# Revit family: ENCBMTYP001
name_source: partatom
category: Furniture
units: mm (PartAtom-declared; Revit-internal decimal feet)

## family parameters
Always vertical = Yes
Cut with Voids When Loaded = No
OmniClass Number = 23.40.20.00
OmniClass Title = General Furniture and Specialties
Render Appearance Source = Family Geometry
Room Calculation Point = No
Shared = No
Work Plane-Based = No

## types (1)
- ENCBMTYP001
    Default Elevation = 0 mm  [stored 0 ft]
    Description = 2 x PASS THROUGH JUMPER - AO2 8W4C - 39"(PASS THRU 30"PANEL, 6 x Black DUPLEX OUTLET LINE 1 - 8W 4C - W/SCREW, 6 x Black DUPLEX OUTLET LINE 2 - 8W 4C - W/SCREW, 1 x BASE INFEED - AO2/MWALL - 8 WIRE 4 CIRCUIT - SIDE MOUNTED, 3 x SPINE SCREEN  50H HORIZON 20H 60W, 6 x Mobile Pedestal - B/F - 24D, 3 x Encounter PwrBeam Double Sided Powered Spine Kit 60, 6 x Encounter PwrBeam Power Cord Tray 60w, 2 x Encounter PwrBeam Raceway Endcap Painted, 4 x Encounter PwrBeam 18 inch T-Leg for 21h, 1 x Encounter PwrBeam UnderMnt pole for 21h, 6 x TBL, REC, 2mm, 30Dx60Wx29H, HAL, E SERIES GLD 2 STAGE
    Exported From CET Designer = Yes
    Manufacturer = AIS
    Model = E-HM8W4PJ30
    Show ENCBMTYP001 = Yes
    VisibilityIndex = 0

note: [stored X ft] marks values corroborated as IEEE doubles in the binary element streams (Revit-internal decimal feet)

## geometry (parser evidence)
native form markers: Sweep x3
no freeform markers — native parametric forms only
